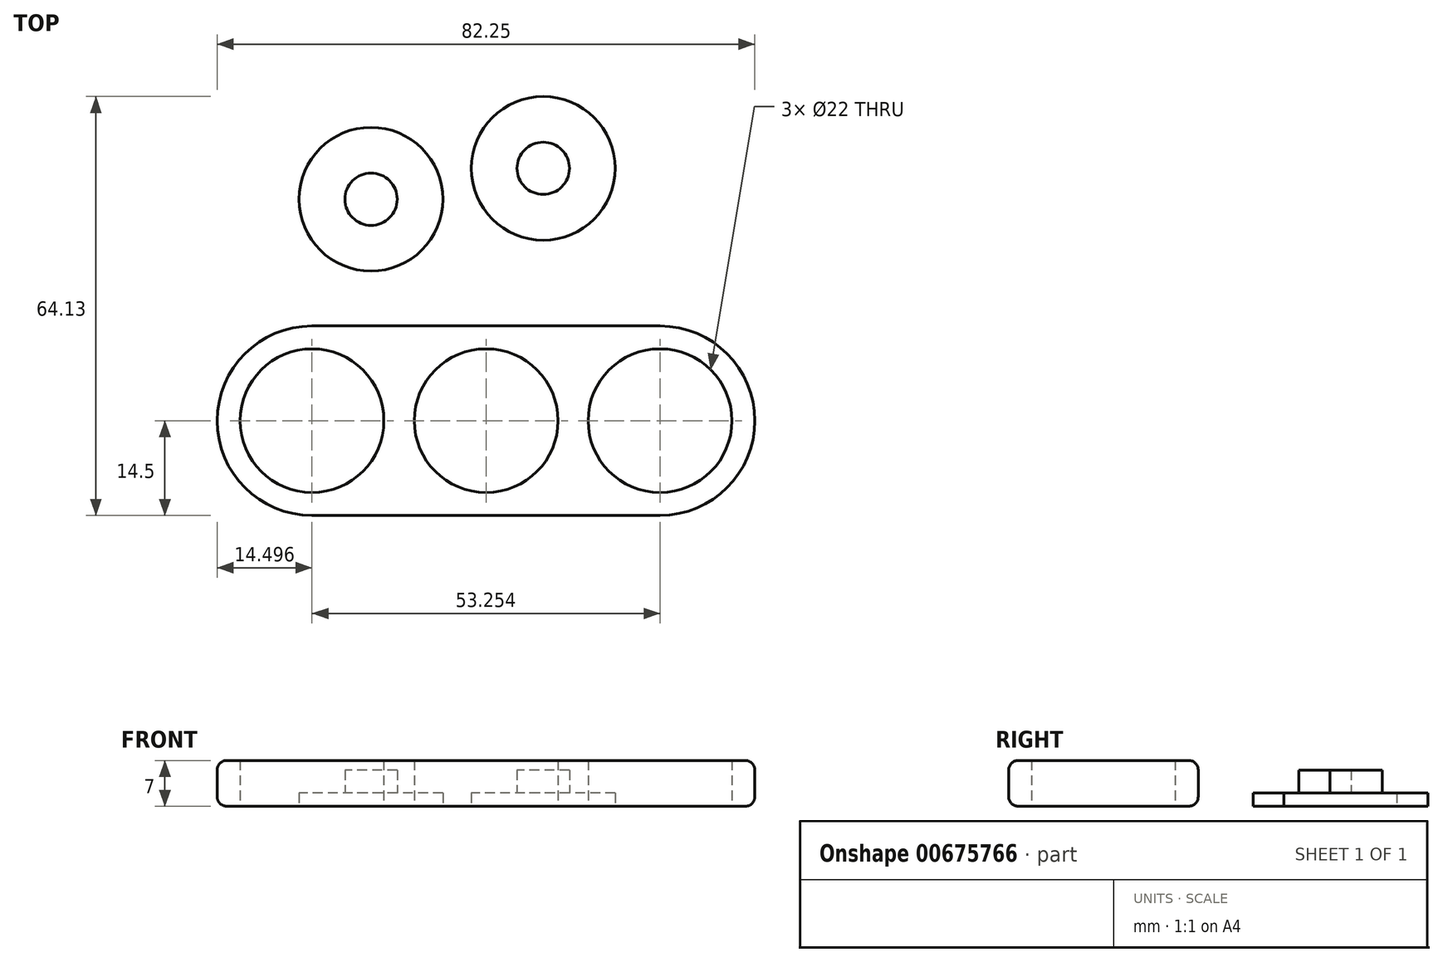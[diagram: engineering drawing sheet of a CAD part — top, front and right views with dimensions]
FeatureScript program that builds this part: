
annotation { "Feature Type Name" : "Feature", "Feature Type Description" : "" }
export const myFeature = defineFeature(function(context is Context, id is Id, definition is map)
    precondition{}
    {
        {
            var Q0;
            Q0=qCreatedBy(makeId("Top.planeOp"),FACE);
            var sketch = newSketch(context, id + "F0", { "sketchPlane" : qUnion([Q0])});
            skCircle(sketch, "E0", {"center": v(0, 0) * mm, "radius": 11 * mm});
            skCircle(sketch, "E1", {"center": v(-26.65, 0) * mm, "radius": 11 * mm});
            skCircle(sketch, "E2.0", {"center": v(-26.65, 0) * mm, "radius": 14.5 * mm});
            skCircle(sketch, "E3", {"center": v(26.6, 0) * mm, "radius": 11 * mm});
            skCircle(sketch, "E4.0", {"center": v(26.6, 0) * mm, "radius": 14.5 * mm});
            skLineSegment(sketch, "E5", {"start": v(-26.65, 14.5) * mm, "end": v(26.6, 14.5) * mm});
            skLineSegment(sketch, "E6", {"start": v(26.6, -14.5) * mm, "end": v(-26.65, -14.5) * mm});
            skSolve(sketch);
        }
        {
            var Q0;
            Q0=makeQuery(id+"F0.imprint","IMPRINT",FACE,{"disambiguationData":[TD([[makeQuery(id+"F0.imprint","IMPRINT",EDGE,{"derivedFrom":sQuery(id+"F0.wireOp",EDGE,"E0")}),-1.0]])]});
            var Q1;
            Q1=makeQuery(id+"F0.imprint","IMPRINT",FACE,{"disambiguationData":[TD([[makeQuery(id+"F0.imprint","IMPRINT",EDGE,{"derivedFrom":sQuery(id+"F0.wireOp",EDGE,"E1")}),-1.0]])]});
            var Q2;
            Q2=makeQuery(id+"F0.imprint","IMPRINT",FACE,{"disambiguationData":[TD([[makeQuery(id+"F0.imprint","IMPRINT",EDGE,{"derivedFrom":sQuery(id+"F0.wireOp",EDGE,"E3")}),-1.0]])]});
            extrude(context, id + "F1", {"entities" : qUnion([Q0, Q1, Q2]), "depth" : 7 * mm, "offsetDistance" : 25 * mm});
        }
        {
            var Q0;
            Q0=makeQuery(id+"F1.opExtrude","CAP_EDGE",EDGE,{"disambiguationData":[OSD([sQuery(id+"F0.wireOp",EDGE,"E5")])],"isStart":false});
            var Q1;
            Q1=makeQuery(id+"F1.opExtrude","CAP_EDGE",EDGE,{"disambiguationData":[OSD([sQuery(id+"F0.wireOp",EDGE,"E2.0")])],"isStart":false});
            var Q2;
            Q2=makeQuery(id+"F1.opExtrude","CAP_EDGE",EDGE,{"disambiguationData":[OSD([sQuery(id+"F0.wireOp",EDGE,"E4.0")])],"isStart":false});
            var Q3;
            Q3=makeQuery(id+"F1.opExtrude","CAP_EDGE",EDGE,{"disambiguationData":[OSD([sQuery(id+"F0.wireOp",EDGE,"E2.0")])],"isStart":true});
            var Q4;
            Q4=makeQuery(id+"F1.opExtrude","CAP_EDGE",EDGE,{"disambiguationData":[OSD([sQuery(id+"F0.wireOp",EDGE,"E6")])],"isStart":true});
            var Q5;
            Q5=makeQuery(id+"F1.opExtrude","CAP_EDGE",EDGE,{"disambiguationData":[OSD([sQuery(id+"F0.wireOp",EDGE,"E4.0")])],"isStart":true});
            fillet(context, id + "F2", {"entities" : qUnion([Q0, Q1, Q2, Q3, Q4, Q5]), "radius" : 1.45 * mm, "tangentPropagation" : true, "allowEdgeOverflow" : false});
        }
        {
            var Q0;
            Q0=qCreatedBy(makeId("Top.planeOp"),FACE);
            var sketch = newSketch(context, id + "F3", { "sketchPlane" : qUnion([Q0])});
            skCircle(sketch, "E7", {"center": v(-17.62, 33.9) * mm, "radius": 11 * mm});
            skSolve(sketch);
        }
        {
            var Q0;
            Q0=makeQuery(id+"F3.imprint","IMPRINT",FACE,{"disambiguationData":[TD([[makeQuery(id+"F3.imprint","IMPRINT",EDGE,{"derivedFrom":sQuery(id+"F3.wireOp",EDGE,"E7")}),1.0]])]});
            extrude(context, id + "F4", {"entities" : qUnion([Q0]), "depth" : 2 * mm, "offsetDistance" : 25 * mm});
        }
        {
            var Q0;
            Q0=makeQuery(id+"F4.opExtrude","CAP_FACE",FACE,{"disambiguationData":[OSD([sQuery(id+"F3.wireOp",EDGE,"E7")])],"isStart":false});
            var sketch = newSketch(context, id + "F5", { "sketchPlane" : qUnion([Q0])});
            skCircle(sketch, "E8", {"center": v(-17.62, 33.9) * mm, "radius": 4 * mm});
            skSolve(sketch);
        }
        {
            var Q0;
            Q0=makeQuery(id+"F5.imprint","IMPRINT",FACE,{"disambiguationData":[TD([[makeQuery(id+"F5.imprint","IMPRINT",EDGE,{"derivedFrom":sQuery(id+"F5.wireOp",EDGE,"E8")}),1.0]])]});
            extrude(context, id + "F6", {"entities" : qUnion([Q0]), "operationType" : NewBodyOperationType.ADD, "depth" : 3.5 * mm, "offsetDistance" : 25 * mm});
        }
        {
            var Q0;
            Q0=qCreatedBy(makeId("Top.planeOp"),FACE);
            var sketch = newSketch(context, id + "F7", { "sketchPlane" : qUnion([Q0])});
            skCircle(sketch, "E9", {"center": v(8.73, 38.63) * mm, "radius": 11 * mm});
            skSolve(sketch);
        }
        {
            var Q0;
            Q0 = qSketchRegion(id + "F7", true);
            extrude(context, id + "F8", {"entities" : qUnion([Q0]), "depth" : 2 * mm, "offsetDistance" : 25 * mm});
        }
        {
            var Q0;
            Q0=makeQuery(id+"F8.opExtrude","CAP_FACE",FACE,{"disambiguationData":[OSD([sQuery(id+"F7.wireOp",EDGE,"E9")])],"isStart":false});
            var sketch = newSketch(context, id + "F9", { "sketchPlane" : qUnion([Q0])});
            skCircle(sketch, "E10", {"center": v(8.73, 38.63) * mm, "radius": 4 * mm});
            skSolve(sketch);
        }
        {
            var Q0;
            Q0=makeQuery(id+"F9.imprint","IMPRINT",FACE,{"disambiguationData":[TD([[makeQuery(id+"F9.imprint","IMPRINT",EDGE,{"derivedFrom":sQuery(id+"F9.wireOp",EDGE,"E10")}),1.0]])]});
            extrude(context, id + "F10", {"entities" : qUnion([Q0]), "operationType" : NewBodyOperationType.ADD, "depth" : 3.5 * mm, "offsetDistance" : 25 * mm});
        }
    });
